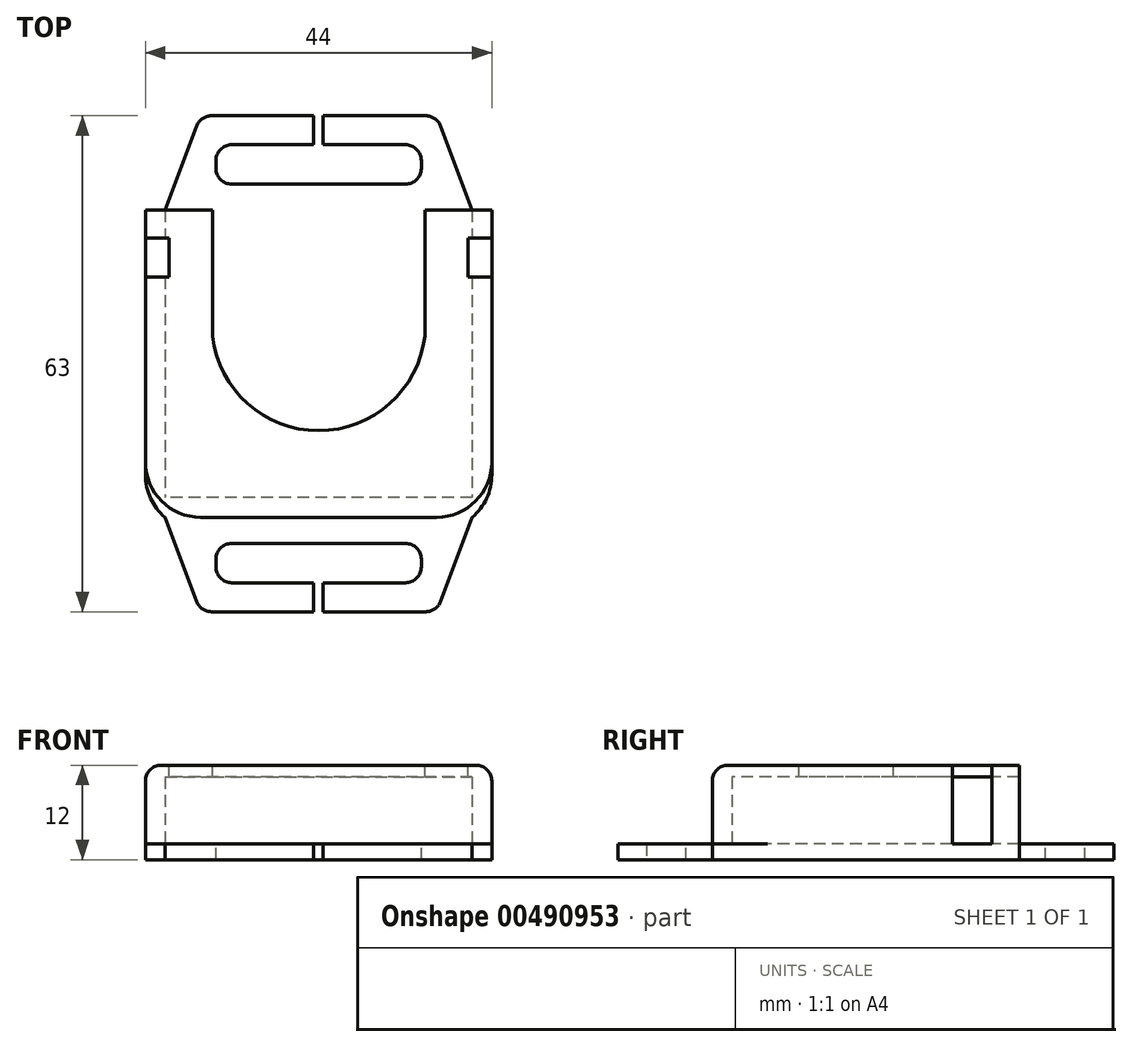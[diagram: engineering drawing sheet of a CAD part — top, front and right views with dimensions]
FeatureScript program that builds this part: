
annotation { "Feature Type Name" : "Feature", "Feature Type Description" : "" }
export const myFeature = defineFeature(function(context is Context, id is Id, definition is map)
    precondition{}
    {
        {
            var Q0;
            Q0=qCreatedBy(makeId("Top.planeOp"),FACE);
            var sketch = newSketch(context, id + "F0", { "sketchPlane" : qUnion([Q0])});
            skLineSegment(sketch, "E0.bottom", {"start": v(22, 19.5) * mm, "end": v(-22, 19.5) * mm});
            skLineSegment(sketch, "E0.top", {"start": v(22, -19.5) * mm, "end": v(-22, -19.5) * mm});
            skLineSegment(sketch, "E0.left", {"start": v(22, 19.5) * mm, "end": v(22, -19.5) * mm});
            skLineSegment(sketch, "E0.right", {"start": v(-22, 19.5) * mm, "end": v(-22, -19.5) * mm});
            skPoint(sketch, "E0.middle", {"position": v(0, 0) * mm});
            skLineSegment(sketch, "E1.0", {"start": v(19.5, 19.5) * mm, "end": v(19.5, -17) * mm});
            skLineSegment(sketch, "E1.1", {"start": v(19.5, -17) * mm, "end": v(-19.5, -17) * mm});
            skLineSegment(sketch, "E1.2", {"start": v(-19.5, 19.5) * mm, "end": v(-19.5, -17) * mm});
            skLineSegment(sketch, "E2", {"start": v(-15, 31.5) * mm, "end": v(15, 31.5) * mm});
            skLineSegment(sketch, "E3.MirrorCS", {"start": v(-15, -31.5) * mm, "end": v(15, -31.5) * mm});
            skLineSegment(sketch, "E4.bottom", {"start": v(13.04, 27.82) * mm, "end": v(-13.04, 27.82) * mm});
            skLineSegment(sketch, "E4.top", {"start": v(13.04, 22.82) * mm, "end": v(-13.04, 22.82) * mm});
            skLineSegment(sketch, "E4.left", {"start": v(13.04, 27.82) * mm, "end": v(13.04, 22.82) * mm});
            skLineSegment(sketch, "E4.right", {"start": v(-13.04, 27.82) * mm, "end": v(-13.04, 22.82) * mm});
            skPoint(sketch, "E4.middle", {"position": v(0, 25.32) * mm});
            skLineSegment(sketch, "E5.MirrorCS", {"start": v(13.04, -22.82) * mm, "end": v(-13.04, -22.82) * mm});
            skLineSegment(sketch, "E6.MirrorCS", {"start": v(13.04, -27.82) * mm, "end": v(-13.04, -27.82) * mm});
            skLineSegment(sketch, "E7.MirrorCS", {"start": v(-13.04, -27.82) * mm, "end": v(-13.04, -22.82) * mm});
            skLineSegment(sketch, "E8.MirrorCS", {"start": v(13.04, -27.82) * mm, "end": v(13.04, -22.82) * mm});
            skLineSegment(sketch, "E9", {"start": v(15, 31.5) * mm, "end": v(19.5, 19.5) * mm});
            skLineSegment(sketch, "E10.MirrorCS", {"start": v(-15, 31.5) * mm, "end": v(-19.5, 19.5) * mm});
            skLineSegment(sketch, "E11.MirrorCS", {"start": v(-15, -31.5) * mm, "end": v(-19.5, -19.5) * mm});
            skLineSegment(sketch, "E12.MirrorCS", {"start": v(15, -31.5) * mm, "end": v(19.5, -19.5) * mm});
            skPoint(sketch, "E13.MirrorCS.start.orphan", {"position": v(15, 19.5) * mm});
            skPoint(sketch, "E14.start.orphan", {"position": v(-15, 19.5) * mm});
            skPoint(sketch, "E15.MirrorCS.end.orphan", {"position": v(-15, -31.5) * mm});
            skPoint(sketch, "E15.MirrorCS.start.orphan", {"position": v(-15, -19.5) * mm});
            skPoint(sketch, "E16.MirrorCS.end.orphan", {"position": v(15, -31.5) * mm});
            skPoint(sketch, "E16.MirrorCS.start.orphan", {"position": v(15, -19.5) * mm});
            skSolve(sketch);
        }
        {
            var Q0;
            Q0=makeQuery(id+"F0.imprint","IMPRINT",FACE,{"disambiguationData":[TD([[makeQuery(id+"F0.imprint","IMPRINT",EDGE,{"derivedFrom":sQuery(id+"F0.wireOp",EDGE,"E0.top")}),-1.0]])]});
            extrude(context, id + "F1", {"entities" : qUnion([Q0]), "depth" : 8.5 * mm});
        }
        {
            var Q0;
            {var subQ0=sQuery(id+"F0.wireOp",EDGE,"E1.0");Q0=makeQuery(id+"F0.imprint","IMPRINT",FACE,{"disambiguationData":[TD([[makeQuery(id+"F0.imprint","IMPRINT",EDGE,{"derivedFrom":subQ0}),-1.0]])]});}
            var Q1;
            Q1=makeQuery(id+"F0.imprint","IMPRINT",FACE,{"disambiguationData":[TD([[makeQuery(id+"F0.imprint","IMPRINT",EDGE,{"derivedFrom":sQuery(id+"F0.wireOp",EDGE,"E0.top")}),-1.0]])]});
            extrude(context, id + "F2", {"entities" : qUnion([Q0, Q1]), "operationType" : NewBodyOperationType.ADD, "oppositeDirection" : true, "depth" : 1.5 * mm});
        }
        {
            var Q0;
            Q0=makeQuery(id+"F1.opExtrude","CAP_FACE",FACE,{"disambiguationData":[OSD([sQuery(id+"F0.wireOp",EDGE,"E0.bottom"),sQuery(id+"F0.wireOp",EDGE,"E0.top"),sQuery(id+"F0.wireOp",EDGE,"E0.left"),sQuery(id+"F0.wireOp",EDGE,"E0.right"),sQuery(id+"F0.wireOp",EDGE,"E1.0"),sQuery(id+"F0.wireOp",EDGE,"E1.1"),sQuery(id+"F0.wireOp",EDGE,"E1.2")])],"isStart":false});
            var sketch = newSketch(context, id + "F3", { "sketchPlane" : qUnion([Q0])});
            skLineSegment(sketch, "E17.bottom", {"start": v(-22, 19.5) * mm, "end": v(22, 19.5) * mm});
            skLineSegment(sketch, "E17.top", {"start": v(-22, -19.5) * mm, "end": v(22, -19.5) * mm});
            skLineSegment(sketch, "E17.left", {"start": v(-22, 19.5) * mm, "end": v(-22, -19.5) * mm});
            skLineSegment(sketch, "E17.right", {"start": v(22, 19.5) * mm, "end": v(22, -19.5) * mm});
            skSolve(sketch);
        }
        {
            var Q0;
            Q0 = qSketchRegion(id + "F3", true);
            extrude(context, id + "F4", {"entities" : qUnion([Q0]), "operationType" : NewBodyOperationType.ADD, "depth" : 1.5 * mm});
        }
        {
            var Q0;
            Q0=makeQuery(id+"F4.opExtrude","CAP_FACE",FACE,{"disambiguationData":[OSD([sQuery(id+"F3.wireOp",EDGE,"E17.bottom"),sQuery(id+"F3.wireOp",EDGE,"E17.top"),sQuery(id+"F3.wireOp",EDGE,"E17.left"),sQuery(id+"F3.wireOp",EDGE,"E17.right")])],"isStart":false});
            var sketch = newSketch(context, id + "F5", { "sketchPlane" : qUnion([Q0])});
            skLineSegment(sketch, "E18", {"start": v(0, 32.5) * mm, "end": v(0, -28.74) * mm, "construction": true});
            skLineSegment(sketch, "E19", {"start": v(-38.3, 0) * mm, "end": v(39.5, 0) * mm, "construction": true});
            skLineSegment(sketch, "E20", {"start": v(13.5, 19.5) * mm, "end": v(13.5, 3.5) * mm});
            skLineSegment(sketch, "E21.MirrorCS", {"start": v(-13.5, 19.5) * mm, "end": v(-13.5, 3.5) * mm});
            skPoint(sketch, "E22", {"position": v(-13.5, 3.5) * mm});
            skPoint(sketch, "E23.MirrorP", {"position": v(13.5, 3.5) * mm});
            skPoint(sketch, "E24", {"position": v(0, -8.5) * mm});
            skArc(sketch, "E25", {"start": v(-13.5, 3.5) * mm, "mid": v(0, -8.5) * mm, "end": v(13.5, 3.5) * mm});
            skPoint(sketch, "E26.orphan", {"position": v(13.5, -13.25) * mm});
            skPoint(sketch, "E27.orphan", {"position": v(-13.5, -13.25) * mm});
            skSolve(sketch);
        }
        {
            var Q0;
            Q0 = qSketchRegion(id + "F5", true);
            var Q1;
            {var subQ0=sQuery(id+"F5.wireOp",EDGE,"E20");Q1=makeQuery(id+"F5.imprint","IMPRINT",FACE,{"disambiguationData":[TD([[makeQuery(id+"F5.imprint","IMPRINT",EDGE,{"derivedFrom":subQ0}),-1.0]])]});}
            extrude(context, id + "F6", {"entities" : qUnion([Q0, Q1]), "operationType" : NewBodyOperationType.REMOVE, "oppositeDirection" : true, "depth" : 2 * mm});
        }
        {
            var Q0;
            Q0=makeQuery(id+"F4.opExtrude","CAP_FACE",FACE,{"disambiguationData":[OSD([sQuery(id+"F3.wireOp",EDGE,"E17.bottom"),sQuery(id+"F3.wireOp",EDGE,"E17.top"),sQuery(id+"F3.wireOp",EDGE,"E17.left"),sQuery(id+"F3.wireOp",EDGE,"E17.right")])],"isStart":false});
            var sketch = newSketch(context, id + "F7", { "sketchPlane" : qUnion([Q0])});
            skLineSegment(sketch, "E28.bottom", {"start": v(22, 16) * mm, "end": v(19, 16) * mm});
            skLineSegment(sketch, "E28.top", {"start": v(22, 11) * mm, "end": v(19, 11) * mm});
            skLineSegment(sketch, "E28.left", {"start": v(22, 16) * mm, "end": v(22, 11) * mm});
            skLineSegment(sketch, "E28.right", {"start": v(19, 16) * mm, "end": v(19, 11) * mm});
            skLineSegment(sketch, "E29.MirrorCS", {"start": v(-22, 16) * mm, "end": v(-22, 11) * mm});
            skLineSegment(sketch, "E30.MirrorCS", {"start": v(-22, 16) * mm, "end": v(-19, 16) * mm});
            skLineSegment(sketch, "E31.MirrorCS", {"start": v(-22, 11) * mm, "end": v(-19, 11) * mm});
            skLineSegment(sketch, "E32.MirrorCS", {"start": v(-19, 16) * mm, "end": v(-19, 11) * mm});
            skSolve(sketch);
        }
        {
            var Q0;
            Q0 = qSketchRegion(id + "F7", true);
            extrude(context, id + "F8", {"entities" : qUnion([Q0]), "operationType" : NewBodyOperationType.REMOVE, "oppositeDirection" : true, "depth" : 10 * mm});
        }
        {
            var Q0;
            {var subQ0=sQuery(id+"F0.wireOp",EDGE,"E0.left");var subQ1=sQuery(id+"F0.wireOp",EDGE,"E0.top");Q0=makeQuery(id+"F4.boolean.opBoolean","MERGE",EDGE,{"derivedFrom":[makeQuery(id+"F2.boolean.opBoolean","MERGE",EDGE,{"derivedFrom":[makeQuery(id+"F1.opExtrude","SWEPT_EDGE",EDGE,{"disambiguationData":[OSD([subQ1,subQ0])]}),makeQuery(id+"F2.opExtrude","SWEPT_EDGE",EDGE,{"disambiguationData":[OSD([subQ1,subQ0])]})]}),makeQuery(id+"F4.opExtrude","SWEPT_EDGE",EDGE,{"disambiguationData":[OSD([sQuery(id+"F3.wireOp",EDGE,"E17.top"),sQuery(id+"F3.wireOp",EDGE,"E17.right")])]})]});}
            var Q1;
            {var subQ0=sQuery(id+"F0.wireOp",EDGE,"E0.right");var subQ1=sQuery(id+"F0.wireOp",EDGE,"E0.top");Q1=makeQuery(id+"F4.boolean.opBoolean","MERGE",EDGE,{"derivedFrom":[makeQuery(id+"F2.boolean.opBoolean","MERGE",EDGE,{"derivedFrom":[makeQuery(id+"F1.opExtrude","SWEPT_EDGE",EDGE,{"disambiguationData":[OSD([subQ1,subQ0])]}),makeQuery(id+"F2.opExtrude","SWEPT_EDGE",EDGE,{"disambiguationData":[OSD([subQ1,subQ0])]})]}),makeQuery(id+"F4.opExtrude","SWEPT_EDGE",EDGE,{"disambiguationData":[OSD([sQuery(id+"F3.wireOp",EDGE,"E17.top"),sQuery(id+"F3.wireOp",EDGE,"E17.left")])]})]});}
            fillet(context, id + "F9", {"entities" : qUnion([Q0, Q1]), "radius" : 7 * mm, "tangentPropagation" : true, "allowEdgeOverflow" : false});
        }
        {
            var Q0;
            {var subQ1=sQuery(id+"F0.wireOp",EDGE,"E0.top");var subQ2=sQuery(id+"F3.wireOp",EDGE,"E17.left");Q0=makeQuery(id+"F8.boolean.opBoolean","SPLIT",EDGE,{"disambiguationData":[TD([makeQuery(id+"F1.opExtrude","SWEPT_FACE",FACE,{"disambiguationData":[OSD([subQ1])]})])],"derivedFrom":makeQuery(id+"F4.opExtrude","CAP_EDGE",EDGE,{"disambiguationData":[OSD([subQ2])],"isStart":false})});}
            var Q1;
            {var subQ0=sQuery(id+"F0.wireOp",EDGE,"E0.bottom");var subQ2=sQuery(id+"F3.wireOp",EDGE,"E17.left");Q1=makeQuery(id+"F8.boolean.opBoolean","SPLIT",EDGE,{"disambiguationData":[TD([makeQuery(id+"F2.opExtrude","SWEPT_FACE",FACE,{"disambiguationData":[OSD([subQ0])]})])],"derivedFrom":makeQuery(id+"F4.opExtrude","CAP_EDGE",EDGE,{"disambiguationData":[OSD([subQ2])],"isStart":false})});}
            var Q2;
            {var subQ0=sQuery(id+"F3.wireOp",EDGE,"E17.left");var subQ1=sQuery(id+"F3.wireOp",EDGE,"E17.top");var subQ2=sQuery(id+"F0.wireOp",EDGE,"E0.right");var subQ3=sQuery(id+"F0.wireOp",EDGE,"E0.top");Q2=makeQuery(id+"F9.opFillet","BLEND_EDGE",EDGE,{"blendedFrom":[makeQuery(id+"F4.boolean.opBoolean","MERGE",EDGE,{"derivedFrom":[makeQuery(id+"F2.boolean.opBoolean","MERGE",EDGE,{"derivedFrom":[makeQuery(id+"F1.opExtrude","SWEPT_EDGE",EDGE,{"disambiguationData":[OSD([subQ3,subQ2])]}),makeQuery(id+"F2.opExtrude","SWEPT_EDGE",EDGE,{"disambiguationData":[OSD([subQ3,subQ2])]})]}),makeQuery(id+"F4.opExtrude","SWEPT_EDGE",EDGE,{"disambiguationData":[OSD([subQ1,subQ0])]})]}),makeQuery(id+"F4.opExtrude","CAP_FACE",FACE,{"disambiguationData":[OSD([sQuery(id+"F3.wireOp",EDGE,"E17.bottom"),subQ1,subQ0,sQuery(id+"F3.wireOp",EDGE,"E17.right")])],"isStart":false})],"blendedInto":[makeQuery(id+"F4.opExtrude","CAP_FACE",FACE,{"disambiguationData":[OSD([sQuery(id+"F3.wireOp",EDGE,"E17.bottom"),subQ1,subQ0,sQuery(id+"F3.wireOp",EDGE,"E17.right")])],"isStart":false})]});}
            var Q3;
            Q3=makeQuery(id+"F4.opExtrude","CAP_EDGE",EDGE,{"disambiguationData":[OSD([sQuery(id+"F3.wireOp",EDGE,"E17.top")])],"isStart":false});
            var Q4;
            {var subQ0=sQuery(id+"F3.wireOp",EDGE,"E17.right");var subQ1=sQuery(id+"F3.wireOp",EDGE,"E17.top");var subQ2=sQuery(id+"F0.wireOp",EDGE,"E0.left");var subQ3=sQuery(id+"F0.wireOp",EDGE,"E0.top");Q4=makeQuery(id+"F9.opFillet","BLEND_EDGE",EDGE,{"blendedFrom":[makeQuery(id+"F4.boolean.opBoolean","MERGE",EDGE,{"derivedFrom":[makeQuery(id+"F2.boolean.opBoolean","MERGE",EDGE,{"derivedFrom":[makeQuery(id+"F1.opExtrude","SWEPT_EDGE",EDGE,{"disambiguationData":[OSD([subQ3,subQ2])]}),makeQuery(id+"F2.opExtrude","SWEPT_EDGE",EDGE,{"disambiguationData":[OSD([subQ3,subQ2])]})]}),makeQuery(id+"F4.opExtrude","SWEPT_EDGE",EDGE,{"disambiguationData":[OSD([subQ1,subQ0])]})]}),makeQuery(id+"F4.opExtrude","CAP_FACE",FACE,{"disambiguationData":[OSD([sQuery(id+"F3.wireOp",EDGE,"E17.bottom"),subQ1,sQuery(id+"F3.wireOp",EDGE,"E17.left"),subQ0])],"isStart":false})],"blendedInto":[makeQuery(id+"F4.opExtrude","CAP_FACE",FACE,{"disambiguationData":[OSD([sQuery(id+"F3.wireOp",EDGE,"E17.bottom"),subQ1,sQuery(id+"F3.wireOp",EDGE,"E17.left"),subQ0])],"isStart":false})]});}
            var Q5;
            {var subQ1=sQuery(id+"F0.wireOp",EDGE,"E0.top");var subQ2=sQuery(id+"F3.wireOp",EDGE,"E17.right");Q5=makeQuery(id+"F8.boolean.opBoolean","SPLIT",EDGE,{"disambiguationData":[TD([makeQuery(id+"F1.opExtrude","SWEPT_FACE",FACE,{"disambiguationData":[OSD([subQ1])]})])],"derivedFrom":makeQuery(id+"F4.opExtrude","CAP_EDGE",EDGE,{"disambiguationData":[OSD([subQ2])],"isStart":false})});}
            var Q6;
            {var subQ0=sQuery(id+"F0.wireOp",EDGE,"E0.bottom");var subQ1=sQuery(id+"F3.wireOp",EDGE,"E17.right");Q6=makeQuery(id+"F8.boolean.opBoolean","SPLIT",EDGE,{"disambiguationData":[TD([makeQuery(id+"F2.opExtrude","SWEPT_FACE",FACE,{"disambiguationData":[OSD([subQ0])]})])],"derivedFrom":makeQuery(id+"F4.opExtrude","CAP_EDGE",EDGE,{"disambiguationData":[OSD([subQ1])],"isStart":false})});}
            fillet(context, id + "F10", {"entities" : qUnion([Q0, Q1, Q2, Q3, Q4, Q5, Q6]), "radius" : 2 * mm, "tangentPropagation" : true, "allowEdgeOverflow" : false});
        }
        {
            var Q0;
            Q0 = qSketchRegion(id + "F0", true);
            extrude(context, id + "F11", {"entities" : qUnion([Q0]), "operationType" : NewBodyOperationType.ADD, "oppositeDirection" : true, "depth" : 2 * mm});
        }
        {
            var Q0;
            Q0=makeQuery(id+"F11.opExtrude","SWEPT_EDGE",EDGE,{"disambiguationData":[OSD([sQuery(id+"F0.wireOp",EDGE,"E0.top"),sQuery(id+"F0.wireOp",EDGE,"E0.right")])]});
            var Q1;
            Q1=makeQuery(id+"F11.opExtrude","SWEPT_EDGE",EDGE,{"disambiguationData":[OSD([sQuery(id+"F0.wireOp",EDGE,"E0.top"),sQuery(id+"F0.wireOp",EDGE,"E0.left")])]});
            fillet(context, id + "F12", {"entities" : qUnion([Q0, Q1]), "radius" : 7 * mm, "tangentPropagation" : true, "allowEdgeOverflow" : false});
        }
        {
            var Q0;
            Q0=makeQuery(id+"F11.opExtrude","SWEPT_EDGE",EDGE,{"disambiguationData":[OSD([sQuery(id+"F0.wireOp",EDGE,"E2"),sQuery(id+"F0.wireOp",EDGE,"E9")])]});
            var Q1;
            Q1=makeQuery(id+"F11.opExtrude","SWEPT_EDGE",EDGE,{"disambiguationData":[OSD([sQuery(id+"F0.wireOp",EDGE,"E0.bottom"),sQuery(id+"F0.wireOp",EDGE,"E1.0"),sQuery(id+"F0.wireOp",EDGE,"E9")])]});
            var Q2;
            Q2=makeQuery(id+"F11.opExtrude","SWEPT_EDGE",EDGE,{"disambiguationData":[OSD([sQuery(id+"F0.wireOp",EDGE,"E0.bottom"),sQuery(id+"F0.wireOp",EDGE,"E1.2"),sQuery(id+"F0.wireOp",EDGE,"E10.MirrorCS")])]});
            var Q3;
            Q3=makeQuery(id+"F11.opExtrude","SWEPT_EDGE",EDGE,{"disambiguationData":[OSD([sQuery(id+"F0.wireOp",EDGE,"E2"),sQuery(id+"F0.wireOp",EDGE,"E10.MirrorCS")])]});
            var Q4;
            Q4=makeQuery(id+"F11.opExtrude","SWEPT_EDGE",EDGE,{"disambiguationData":[OSD([sQuery(id+"F0.wireOp",EDGE,"E3.MirrorCS"),sQuery(id+"F0.wireOp",EDGE,"E12.MirrorCS")])]});
            var Q5;
            Q5=makeQuery(id+"F11.opExtrude","SWEPT_EDGE",EDGE,{"disambiguationData":[OSD([sQuery(id+"F0.wireOp",EDGE,"E3.MirrorCS"),sQuery(id+"F0.wireOp",EDGE,"E11.MirrorCS")])]});
            fillet(context, id + "F13", {"entities" : qUnion([Q0, Q1, Q2, Q3, Q4, Q5]), "radius" : 2 * mm, "tangentPropagation" : true, "allowEdgeOverflow" : false});
        }
        {
            var Q0;
            Q0=makeQuery(id+"F11.opExtrude","SWEPT_EDGE",EDGE,{"disambiguationData":[OSD([sQuery(id+"F0.wireOp",EDGE,"E4.top"),sQuery(id+"F0.wireOp",EDGE,"E4.right")])]});
            var Q1;
            Q1=makeQuery(id+"F11.opExtrude","SWEPT_EDGE",EDGE,{"disambiguationData":[OSD([sQuery(id+"F0.wireOp",EDGE,"E4.bottom"),sQuery(id+"F0.wireOp",EDGE,"E4.right")])]});
            var Q2;
            Q2=makeQuery(id+"F11.opExtrude","SWEPT_EDGE",EDGE,{"disambiguationData":[OSD([sQuery(id+"F0.wireOp",EDGE,"E4.bottom"),sQuery(id+"F0.wireOp",EDGE,"E4.left")])]});
            var Q3;
            Q3=makeQuery(id+"F11.opExtrude","SWEPT_EDGE",EDGE,{"disambiguationData":[OSD([sQuery(id+"F0.wireOp",EDGE,"E4.top"),sQuery(id+"F0.wireOp",EDGE,"E4.left")])]});
            var Q4;
            Q4=makeQuery(id+"F11.opExtrude","SWEPT_EDGE",EDGE,{"disambiguationData":[OSD([sQuery(id+"F0.wireOp",EDGE,"E6.MirrorCS"),sQuery(id+"F0.wireOp",EDGE,"E8.MirrorCS")])]});
            var Q5;
            Q5=makeQuery(id+"F11.opExtrude","SWEPT_EDGE",EDGE,{"disambiguationData":[OSD([sQuery(id+"F0.wireOp",EDGE,"E5.MirrorCS"),sQuery(id+"F0.wireOp",EDGE,"E8.MirrorCS")])]});
            var Q6;
            Q6=makeQuery(id+"F11.opExtrude","SWEPT_EDGE",EDGE,{"disambiguationData":[OSD([sQuery(id+"F0.wireOp",EDGE,"E5.MirrorCS"),sQuery(id+"F0.wireOp",EDGE,"E7.MirrorCS")])]});
            var Q7;
            Q7=makeQuery(id+"F11.opExtrude","SWEPT_EDGE",EDGE,{"disambiguationData":[OSD([sQuery(id+"F0.wireOp",EDGE,"E6.MirrorCS"),sQuery(id+"F0.wireOp",EDGE,"E7.MirrorCS")])]});
            fillet(context, id + "F14", {"entities" : qUnion([Q0, Q1, Q2, Q3, Q4, Q5, Q6, Q7]), "radius" : 2 * mm, "tangentPropagation" : true, "allowEdgeOverflow" : false});
        }
        {
            var Q0;
            Q0=makeQuery(id+"F0.imprint","IMPRINT",FACE,{"disambiguationData":[TD([[makeQuery(id+"F0.imprint","IMPRINT",EDGE,{"derivedFrom":sQuery(id+"F0.wireOp",EDGE,"E2")}),-1.0]])]});
            var sketch = newSketch(context, id + "F15", { "sketchPlane" : qUnion([Q0])});
            skLineSegment(sketch, "E33.bottom", {"start": v(-0.63, 31.53) * mm, "end": v(0.57, 31.53) * mm});
            skLineSegment(sketch, "E33.top", {"start": v(-0.63, 27.79) * mm, "end": v(0.57, 27.79) * mm});
            skLineSegment(sketch, "E33.left", {"start": v(-0.63, 31.53) * mm, "end": v(-0.63, 27.79) * mm});
            skLineSegment(sketch, "E33.right", {"start": v(0.57, 31.53) * mm, "end": v(0.57, 27.79) * mm});
            skLineSegment(sketch, "E34.MirrorCS", {"start": v(-0.63, -31.53) * mm, "end": v(-0.63, -27.79) * mm});
            skLineSegment(sketch, "E35.MirrorCS", {"start": v(-0.63, -31.53) * mm, "end": v(0.57, -31.53) * mm});
            skLineSegment(sketch, "E36.MirrorCS", {"start": v(0.57, -31.53) * mm, "end": v(0.57, -27.79) * mm});
            skLineSegment(sketch, "E37.MirrorCS", {"start": v(-0.63, -27.79) * mm, "end": v(0.57, -27.79) * mm});
            skSolve(sketch);
        }
        {
            var Q0;
            Q0 = qSketchRegion(id + "F15", true);
            extrude(context, id + "F16", {"entities" : qUnion([Q0]), "operationType" : NewBodyOperationType.REMOVE, "oppositeDirection" : true, "depth" : 5 * mm});
        }
    });
